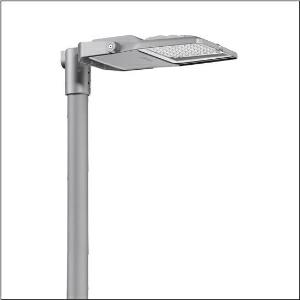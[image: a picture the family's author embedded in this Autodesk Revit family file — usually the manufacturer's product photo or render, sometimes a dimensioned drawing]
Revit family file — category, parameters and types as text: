
# Revit family: floodlight_fl_21_iq_mini___pl52_5xa7772d4d3a_25ab
name_source: partatom
category: Lighting Fixtures
units: mm (PartAtom-declared; Revit-internal decimal feet)

## family parameters
Cut with Voids When Loaded = No
Host = Face
Light Source = No
Part Type = Normal
Room Calculation Point = No
Round Connector Dimension = Use Diameter
Shared = No

## types (1)
- --- (1 x LED, 18610 lm, 143 W, 4000K)
    Apparent Load = 143 VA
    CIE Flux Codes = 26 60 98 100 100
    Color Rendering = 70
    Color Temperature = 4000K
    Default Elevation = 1800 mm
    Description = Floodlight FL 21 iQ mini, floodlight, primary light control with lens, of PMMA, primary optical cover: protective disc, of toughened safety glass, transparent, light distribution: PL52, light emission: direct distribution, installation type: surface-mounted, LED, High Power LED, rated luminous flux: 18.610lm, luminous efficacy: 130lm/W, light colour: 740, colour temperature: 4000K, control: Auto-Match, Temp-Guard, Night-Set, Smart-Wire, Desk-Remote (wireless, voltage-free reading and setting of iQ features in the workshop via application-optimized NFC function/RFID function), optimised constant luminous flux control (CLO 2.0), Light-Fading, Lumen-Switch, with terminal, 6-pole, mains connection: 220..240V, AC, 50/60Hz, start of lifetime: 143W, end of service life: 152W, reduction: 61W, luminaire housing, of diecast aluminium, powder-coated, Siteco® metallic grey (DB 702S), corrosivity category C5 mid according to DIN EN ISO 12944, sealing non-destructively replaceable, please order mast flange separately, mast bracket, of steel, galvanised, powder-coated, protection rating (complete): IP66, insulation class (complete): insulation class II (safety insulation), certification: CE, ENEC, VDE, protection symbol: D, impact resistance: IK08, permissible operating ambient temperature: -40..+40°C, permissible operating ambient temperature for outdoor applications: -40..+50°C, standard: DIN EN 12944, LABS conformity tested according to VDMA 24364:2018-05, packaging unit: 1 piece

Light Distribution: PL52
    Height = 70 mm
    Lamp = 1 x LED
    Lamp Light Flux = 18610 lm
    Lamp Power = 143 W
    Lamp count = 1
    Length = 485 mm
    Luminous efficacy = 130 lm/W
    Manufacturer = Siteco
    ModVariant = No
    Model = 5XA7772D4D3A
    Number of Poles = 1
    OnlyDefault = Yes
    Power Factor = 1
    Product Name = Floodlight FL 21 iQ mini | PL52
    Product group = floodlight | pylon annexe
    ProductGroupID = 6200
    Protection Class = Protection class II
    Protection Degree = IP 66
    RLX_Detail_Level = 1
    RLX_Emergency_Light_Flux = 0 lm
    RLX_Emergency_Type = 0
    RLX_Emergency_Type_DB = No
    RlxData = <blob elided: 101737 chars, md5=4e7059f7>
    Socket = socket
    Standby Power = 0 W
    System Light Flux = 18610 lm
    System Power = 143 W
    Type Comments = factory setting: luminous flux: 100 % | dim-lin: 254 | 730 mA
    Type Image = l_1007125.jpg
    URL = http://relux.com
    VarID = @adj_133893
    Voltage = 0 V
    Weight = 0.00 kg
    Width = 337 mm

## geometry (parser evidence)
native form markers: Blend x4, Sweep x11
no freeform markers — native parametric forms only
